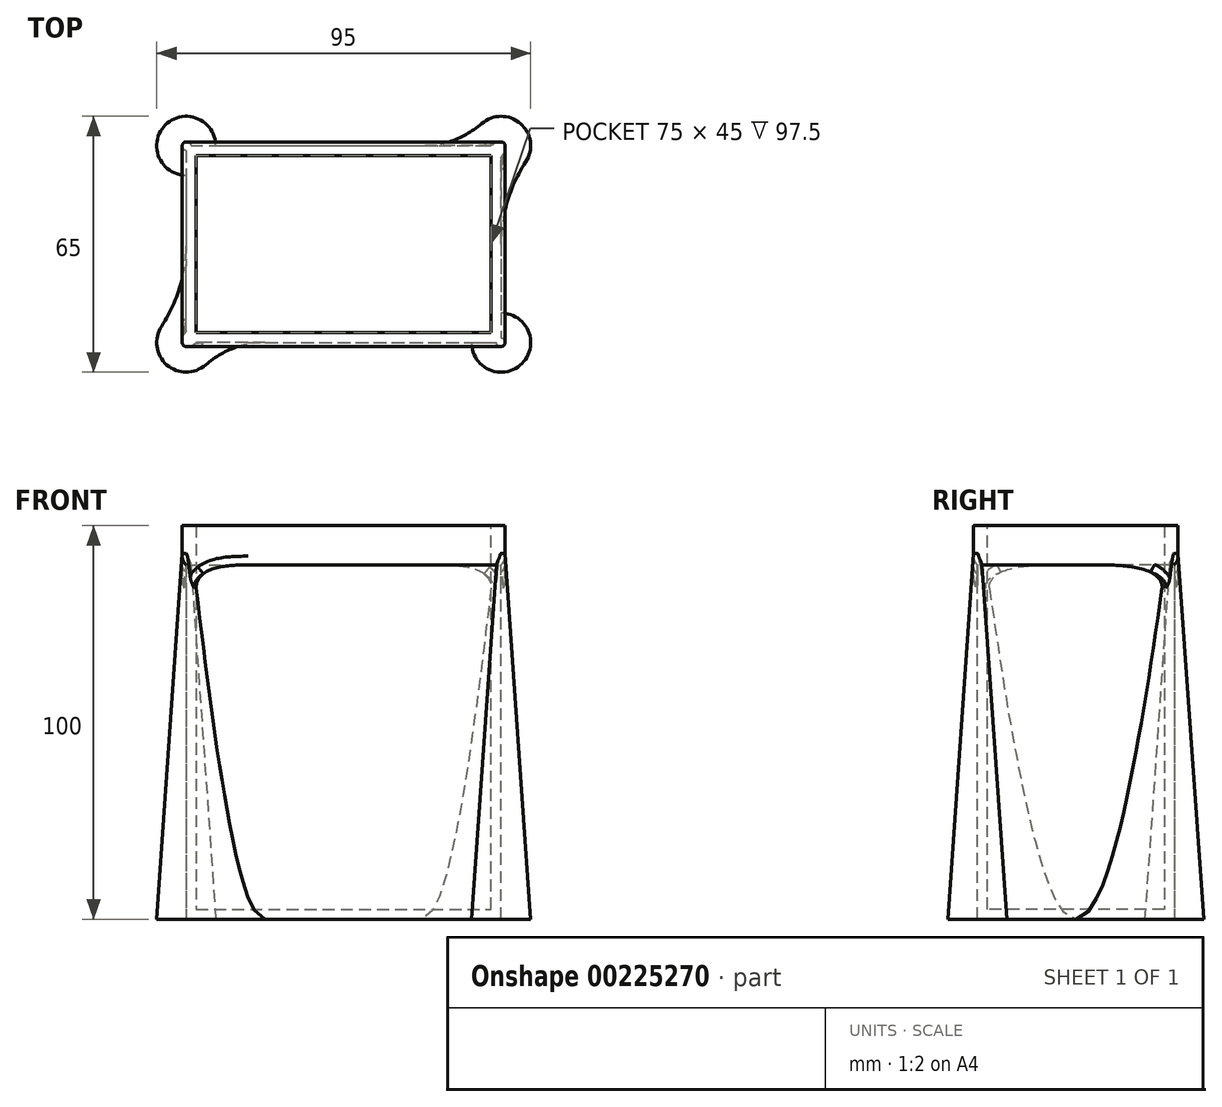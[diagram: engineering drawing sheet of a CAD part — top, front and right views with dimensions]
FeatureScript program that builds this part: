
annotation { "Feature Type Name" : "Feature", "Feature Type Description" : "" }
export const myFeature = defineFeature(function(context is Context, id is Id, definition is map)
    precondition{}
    {
        {
            var Q0;
            Q0=qCreatedBy(makeId("Top.planeOp"),FACE);
            var sketch = newSketch(context, id + "F0", { "sketchPlane" : qUnion([Q0])});
            skLineSegment(sketch, "E0.bottom", {"start": v(-40, 25) * mm, "end": v(40, 25) * mm});
            skLineSegment(sketch, "E0.top", {"start": v(-40, -25) * mm, "end": v(40, -25) * mm});
            skLineSegment(sketch, "E0.left", {"start": v(-40, 25) * mm, "end": v(-40, -25) * mm});
            skLineSegment(sketch, "E0.right", {"start": v(40, 25) * mm, "end": v(40, -25) * mm});
            skPoint(sketch, "E0.middle", {"position": v(0, 0) * mm});
            skSolve(sketch);
        }
        {
            var Q0;
            Q0 = qSketchRegion(id + "F0", true);
            extrude(context, id + "F1", {"entities" : qUnion([Q0]), "depth" : 100 * mm, "offsetDistance" : 25 * mm});
        }
        {
            var Q0;
            Q0=makeQuery(id+"F1.opExtrude","CAP_FACE",FACE,{"disambiguationData":[OSD([sQuery(id+"F0.wireOp",EDGE,"E0.bottom"),sQuery(id+"F0.wireOp",EDGE,"E0.top"),sQuery(id+"F0.wireOp",EDGE,"E0.left"),sQuery(id+"F0.wireOp",EDGE,"E0.right")])],"isStart":false});
            shell(context, id + "F2", {"entities" : qUnion([Q0]), "thickness" : 2.5 * mm});
        }
        {
            var Q0;
            Q0=makeQuery(id+"F1.opExtrude","CAP_FACE",FACE,{"disambiguationData":[OSD([sQuery(id+"F0.wireOp",EDGE,"E0.bottom"),sQuery(id+"F0.wireOp",EDGE,"E0.top"),sQuery(id+"F0.wireOp",EDGE,"E0.left"),sQuery(id+"F0.wireOp",EDGE,"E0.right")])],"isStart":true});
            var sketch = newSketch(context, id + "F3", { "sketchPlane" : qUnion([Q0])});
            skCircle(sketch, "E1", {"center": v(-40, 25) * mm, "radius": 7.5 * mm});
            skLineSegment(sketch, "E2", {"start": v(0, 34.3) * mm, "end": v(0, -35.51) * mm, "construction": true});
            skLineSegment(sketch, "E3", {"start": v(-69.58, 0) * mm, "end": v(52.99, 0) * mm, "construction": true});
            skArc(sketch, "E4", {"start": v(-40, 0) * mm, "mid": v(-41.6, 10.9) * mm, "end": v(-46.26, 20.87) * mm});
            skArc(sketch, "E5", {"start": v(-35.07, 30.65) * mm, "mid": v(-28.05, 26.46) * mm, "end": v(-20, 25) * mm});
            skCircle(sketch, "E6.MirrorC", {"center": v(40, 25) * mm, "radius": 7.5 * mm});
            skArc(sketch, "E7.MirrorCS", {"start": v(35.07, 30.65) * mm, "mid": v(28.05, 26.46) * mm, "end": v(20, 25) * mm});
            skArc(sketch, "E8.MirrorCS", {"start": v(40, 0) * mm, "mid": v(41.6, 10.9) * mm, "end": v(46.26, 20.87) * mm});
            skCircle(sketch, "E9.MirrorC", {"center": v(-40, -25) * mm, "radius": 7.5 * mm});
            skArc(sketch, "E10.MirrorCS", {"start": v(35.07, -30.65) * mm, "mid": v(28.05, -26.46) * mm, "end": v(20, -25) * mm});
            skCircle(sketch, "E11.MirrorC", {"center": v(40, -25) * mm, "radius": 7.5 * mm});
            skArc(sketch, "E12.MirrorCS", {"start": v(40, 0) * mm, "mid": v(41.6, -10.9) * mm, "end": v(46.26, -20.87) * mm});
            skArc(sketch, "E13.MirrorCS", {"start": v(-35.07, -30.65) * mm, "mid": v(-28.05, -26.46) * mm, "end": v(-20, -25) * mm});
            skArc(sketch, "E14.MirrorCS", {"start": v(-40, 0) * mm, "mid": v(-41.6, -10.9) * mm, "end": v(-46.26, -20.87) * mm});
            skSolve(sketch);
        }
        {
            var Q0;
            {var subQ0=makeQuery(id+"F1.opExtrude","CAP_EDGE",EDGE,{"disambiguationData":[OSD([sQuery(id+"F0.wireOp",EDGE,"E0.top")])],"isStart":true});var subQ5=sQuery(id+"F3.wireOp",EDGE,"E1");var subQ6=makeQuery(id+"F3.imprint","INTERSECT",VERTEX,{"derivedFrom":[subQ0,subQ5]});Q0=makeQuery(id+"F3.imprint","IMPRINT",FACE,{"disambiguationData":[TD([[makeQuery(id+"F3.imprint","IMPRINT",EDGE,{"disambiguationData":[TD([[subQ6,1.0]])],"derivedFrom":subQ5}),-1.0]])]});}
            cPlane(context, id + "F4", {"entities" : qUnion([Q0]), "cplaneType" : CPlaneType.OFFSET, "offset" : 67 * mm, "oppositeDirection" : true, "width" : 150 * mm, "height" : 150 * mm});
        }
        {
            var Q0;
            Q0 = qSketchRegion(id + "F3", true);
            var Q1;
            {var subQ0=sQuery(id+"F3.wireOp",EDGE,"E14.MirrorCS");Q1=makeQuery(id+"F3.imprint","IMPRINT",FACE,{"disambiguationData":[TD([[makeQuery(id+"F3.imprint","IMPRINT",EDGE,{"derivedFrom":subQ0}),1.0]])]});}
            var Q2;
            {var subQ0=makeQuery(id+"F1.opExtrude","CAP_EDGE",EDGE,{"disambiguationData":[OSD([sQuery(id+"F0.wireOp",EDGE,"E0.top")])],"isStart":true});var subQ5=sQuery(id+"F3.wireOp",EDGE,"E1");var subQ6=makeQuery(id+"F3.imprint","INTERSECT",VERTEX,{"derivedFrom":[subQ0,subQ5]});Q2=makeQuery(id+"F3.imprint","IMPRINT",FACE,{"disambiguationData":[TD([[makeQuery(id+"F3.imprint","IMPRINT",EDGE,{"disambiguationData":[TD([[subQ6,1.0]])],"derivedFrom":subQ5}),-1.0]])]});}
            var Q3;
            {var subQ0=sQuery(id+"F3.wireOp",EDGE,"E13.MirrorCS");Q3=makeQuery(id+"F3.imprint","IMPRINT",FACE,{"disambiguationData":[TD([[makeQuery(id+"F3.imprint","IMPRINT",EDGE,{"derivedFrom":subQ0}),1.0]])]});}
            var Q4;
            {var subQ0=sQuery(id+"F3.wireOp",EDGE,"E4");Q4=makeQuery(id+"F3.imprint","IMPRINT",FACE,{"disambiguationData":[TD([[makeQuery(id+"F3.imprint","IMPRINT",EDGE,{"derivedFrom":subQ0}),-1.0]])]});}
            var Q5;
            {var subQ0=sQuery(id+"F3.wireOp",EDGE,"E5");Q5=makeQuery(id+"F3.imprint","IMPRINT",FACE,{"disambiguationData":[TD([[makeQuery(id+"F3.imprint","IMPRINT",EDGE,{"derivedFrom":subQ0}),-1.0]])]});}
            var Q6;
            {var subQ0=sQuery(id+"F3.wireOp",EDGE,"E7.MirrorCS");Q6=makeQuery(id+"F3.imprint","IMPRINT",FACE,{"disambiguationData":[TD([[makeQuery(id+"F3.imprint","IMPRINT",EDGE,{"derivedFrom":subQ0}),1.0]])]});}
            var Q7;
            {var subQ0=sQuery(id+"F3.wireOp",EDGE,"E8.MirrorCS");Q7=makeQuery(id+"F3.imprint","IMPRINT",FACE,{"disambiguationData":[TD([[makeQuery(id+"F3.imprint","IMPRINT",EDGE,{"derivedFrom":subQ0}),1.0]])]});}
            var Q8;
            {var subQ0=sQuery(id+"F3.wireOp",EDGE,"E12.MirrorCS");Q8=makeQuery(id+"F3.imprint","IMPRINT",FACE,{"disambiguationData":[TD([[makeQuery(id+"F3.imprint","IMPRINT",EDGE,{"derivedFrom":subQ0}),-1.0]])]});}
            var Q9;
            {var subQ0=sQuery(id+"F3.wireOp",EDGE,"E10.MirrorCS");Q9=makeQuery(id+"F3.imprint","IMPRINT",FACE,{"disambiguationData":[TD([[makeQuery(id+"F3.imprint","IMPRINT",EDGE,{"derivedFrom":subQ0}),-1.0]])]});}
            extrude(context, id + "F5", {"entities" : qUnion([Q0, Q1, Q2, Q3, Q4, Q5, Q6, Q7, Q8, Q9]), "operationType" : NewBodyOperationType.ADD, "oppositeDirection" : true, "depth" : 100 * mm, "offsetDistance" : 25 * mm, "hasDraft" : true, "draftAngle" : 4 * degree, "draftPullDirection" : true});
        }
        {
            var Q0;
            {var subQ0=sQuery(id+"F0.wireOp",EDGE,"E0.top");var subQ1=sQuery(id+"F0.wireOp",EDGE,"E0.bottom");Q0=makeQuery(id+"F5.boolean.opBoolean","MERGE",FACE,{"derivedFrom":[makeQuery(id+"F1.opExtrude","CAP_FACE",FACE,{"disambiguationData":[OSD([subQ1,subQ0,sQuery(id+"F0.wireOp",EDGE,"E0.left"),sQuery(id+"F0.wireOp",EDGE,"E0.right")])],"isStart":false}),makeQuery(id+"F5.opExtrude","CAP_FACE",FACE,{"disambiguationData":[OSD([subQ1,subQ0,sQuery(id+"F3.wireOp",EDGE,"E1"),sQuery(id+"F3.wireOp",EDGE,"E4"),sQuery(id+"F3.wireOp",EDGE,"E5"),sQuery(id+"F3.wireOp",EDGE,"E6.MirrorC"),sQuery(id+"F3.wireOp",EDGE,"E7.MirrorCS"),sQuery(id+"F3.wireOp",EDGE,"E8.MirrorCS"),sQuery(id+"F3.wireOp",EDGE,"E9.MirrorC"),sQuery(id+"F3.wireOp",EDGE,"E10.MirrorCS"),sQuery(id+"F3.wireOp",EDGE,"E11.MirrorC"),sQuery(id+"F3.wireOp",EDGE,"E12.MirrorCS"),sQuery(id+"F3.wireOp",EDGE,"E13.MirrorCS"),sQuery(id+"F3.wireOp",EDGE,"E14.MirrorCS")])],"isStart":false})]});}
            var sketch = newSketch(context, id + "F6", { "sketchPlane" : qUnion([Q0])});
            skLineSegment(sketch, "E15.bottom", {"start": v(-37.5, 22.5) * mm, "end": v(37.5, 22.5) * mm});
            skLineSegment(sketch, "E15.top", {"start": v(-37.5, -22.5) * mm, "end": v(37.5, -22.5) * mm});
            skLineSegment(sketch, "E15.left", {"start": v(-37.5, 22.5) * mm, "end": v(-37.5, -22.5) * mm});
            skLineSegment(sketch, "E15.right", {"start": v(37.5, 22.5) * mm, "end": v(37.5, -22.5) * mm});
            skPoint(sketch, "E15.middle", {"position": v(0, 0) * mm});
            skSolve(sketch);
        }
        {
            var Q0;
            {var subQ11=sQuery(id+"F3.wireOp",EDGE,"E1");Q0=makeQuery(id+"F6.imprint","IMPRINT",FACE,{"disambiguationData":[TD([[makeQuery(id+"F6.imprint","IMPRINT",EDGE,{"derivedFrom":makeQuery(id+"F5.opExtrude","CAP_EDGE",EDGE,{"disambiguationData":[OSD([subQ11])],"isStart":false})}),-1.0]])]});}
            var sketch = newSketch(context, id + "F7", { "sketchPlane" : qUnion([Q0])});
            skLineSegment(sketch, "E16.bottom", {"start": v(-41, 26) * mm, "end": v(41, 26) * mm});
            skLineSegment(sketch, "E16.top", {"start": v(-41, -26) * mm, "end": v(41, -26) * mm});
            skLineSegment(sketch, "E16.left", {"start": v(-41, 26) * mm, "end": v(-41, -26) * mm});
            skLineSegment(sketch, "E16.right", {"start": v(41, 26) * mm, "end": v(41, -26) * mm});
            skSolve(sketch);
        }
        {
            var Q0;
            Q0 = qSketchRegion(id + "F7", true);
            extrude(context, id + "F8", {"entities" : qUnion([Q0]), "operationType" : NewBodyOperationType.ADD, "oppositeDirection" : true, "depth" : 10 * mm, "offsetDistance" : 25 * mm});
        }
        {
            var Q0;
            Q0=makeQuery(id+"F8.opExtrude","SWEPT_EDGE",EDGE,{"disambiguationData":[OSD([sQuery(id+"F7.wireOp",EDGE,"E16.top"),sQuery(id+"F7.wireOp",EDGE,"E16.left")])]});
            var Q1;
            Q1=makeQuery(id+"F8.opExtrude","SWEPT_EDGE",EDGE,{"disambiguationData":[OSD([sQuery(id+"F7.wireOp",EDGE,"E16.bottom"),sQuery(id+"F7.wireOp",EDGE,"E16.left")])]});
            var Q2;
            Q2=makeQuery(id+"F8.opExtrude","SWEPT_EDGE",EDGE,{"disambiguationData":[OSD([sQuery(id+"F7.wireOp",EDGE,"E16.top"),sQuery(id+"F7.wireOp",EDGE,"E16.right")])]});
            var Q3;
            Q3=makeQuery(id+"F8.opExtrude","SWEPT_EDGE",EDGE,{"disambiguationData":[OSD([sQuery(id+"F7.wireOp",EDGE,"E16.bottom"),sQuery(id+"F7.wireOp",EDGE,"E16.right")])]});
            fillet(context, id + "F9", {"entities" : qUnion([Q0, Q1, Q2, Q3]), "radius" : 1 * mm, "tangentPropagation" : true, "allowEdgeOverflow" : false});
        }
        {
            var Q0;
            {var subQ1=sQuery(id+"F3.wireOp",EDGE,"E1");var subQ5=sQuery(id+"F3.wireOp",EDGE,"E14.MirrorCS");var subQ15=sQuery(id+"F3.wireOp",EDGE,"E4");var subQ16=makeQuery(id+"F5.opExtrude","SWEPT_FACE",FACE,{"disambiguationData":[OSD([subQ15,subQ5])]});Q0=makeQuery(id+"F8.boolean.opBoolean","INTERSECT",EDGE,{"derivedFrom":[makeQuery(id+"F5.boolean.opBoolean","SPLIT",FACE,{"disambiguationData":[TD([makeQuery(id+"F5.opExtrude","SWEPT_FACE",FACE,{"disambiguationData":[OSD([subQ1])]})])],"derivedFrom":subQ16}),makeQuery(id+"F8.opExtrude","CAP_FACE",FACE,{"disambiguationData":[OSD([sQuery(id+"F7.wireOp",EDGE,"E16.bottom"),sQuery(id+"F7.wireOp",EDGE,"E16.top"),sQuery(id+"F7.wireOp",EDGE,"E16.left"),sQuery(id+"F7.wireOp",EDGE,"E16.right")])],"isStart":false})]});}
            var Q1;
            {var subQ0=sQuery(id+"F3.wireOp",EDGE,"E14.MirrorCS");var subQ5=sQuery(id+"F3.wireOp",EDGE,"E9.MirrorC");var subQ10=sQuery(id+"F3.wireOp",EDGE,"E4");var subQ16=makeQuery(id+"F5.opExtrude","SWEPT_FACE",FACE,{"disambiguationData":[OSD([subQ10,subQ0])]});Q1=makeQuery(id+"F8.boolean.opBoolean","INTERSECT",EDGE,{"derivedFrom":[makeQuery(id+"F5.boolean.opBoolean","SPLIT",FACE,{"disambiguationData":[TD([makeQuery(id+"F5.opExtrude","SWEPT_FACE",FACE,{"disambiguationData":[OSD([subQ5])]})])],"derivedFrom":subQ16}),makeQuery(id+"F8.opExtrude","CAP_FACE",FACE,{"disambiguationData":[OSD([sQuery(id+"F7.wireOp",EDGE,"E16.bottom"),sQuery(id+"F7.wireOp",EDGE,"E16.top"),sQuery(id+"F7.wireOp",EDGE,"E16.left"),sQuery(id+"F7.wireOp",EDGE,"E16.right")])],"isStart":false})]});}
            var Q2;
            {var subQ7=sQuery(id+"F3.wireOp",EDGE,"E7.MirrorCS");var subQ12=sQuery(id+"F0.wireOp",EDGE,"E0.top");Q2=makeQuery(id+"F8.boolean.opBoolean","INTERSECT",EDGE,{"derivedFrom":[makeQuery(id+"F5.boolean.opBoolean","SPLIT",FACE,{"disambiguationData":[TD([makeQuery(id+"F1.opExtrude","SWEPT_FACE",FACE,{"disambiguationData":[OSD([subQ12])]})])],"derivedFrom":makeQuery(id+"F5.opExtrude","SWEPT_FACE",FACE,{"disambiguationData":[OSD([subQ7])]})}),makeQuery(id+"F8.opExtrude","CAP_FACE",FACE,{"disambiguationData":[OSD([sQuery(id+"F7.wireOp",EDGE,"E16.bottom"),sQuery(id+"F7.wireOp",EDGE,"E16.top"),sQuery(id+"F7.wireOp",EDGE,"E16.left"),sQuery(id+"F7.wireOp",EDGE,"E16.right")])],"isStart":false})]});}
            var Q3;
            {var subQ0=sQuery(id+"F0.wireOp",EDGE,"E0.top");var subQ14=sQuery(id+"F3.wireOp",EDGE,"E5");Q3=makeQuery(id+"F8.boolean.opBoolean","INTERSECT",EDGE,{"derivedFrom":[makeQuery(id+"F5.boolean.opBoolean","SPLIT",FACE,{"disambiguationData":[TD([makeQuery(id+"F1.opExtrude","SWEPT_FACE",FACE,{"disambiguationData":[OSD([subQ0])]})])],"derivedFrom":makeQuery(id+"F5.opExtrude","SWEPT_FACE",FACE,{"disambiguationData":[OSD([subQ14])]})}),makeQuery(id+"F8.opExtrude","CAP_FACE",FACE,{"disambiguationData":[OSD([sQuery(id+"F7.wireOp",EDGE,"E16.bottom"),sQuery(id+"F7.wireOp",EDGE,"E16.top"),sQuery(id+"F7.wireOp",EDGE,"E16.left"),sQuery(id+"F7.wireOp",EDGE,"E16.right")])],"isStart":false})]});}
            var Q4;
            {var subQ2=sQuery(id+"F3.wireOp",EDGE,"E12.MirrorCS");var subQ6=sQuery(id+"F3.wireOp",EDGE,"E8.MirrorCS");var subQ8=sQuery(id+"F3.wireOp",EDGE,"E6.MirrorC");var subQ16=makeQuery(id+"F5.opExtrude","SWEPT_FACE",FACE,{"disambiguationData":[OSD([subQ6,subQ2])]});Q4=makeQuery(id+"F8.boolean.opBoolean","INTERSECT",EDGE,{"derivedFrom":[makeQuery(id+"F5.boolean.opBoolean","SPLIT",FACE,{"disambiguationData":[TD([makeQuery(id+"F5.opExtrude","SWEPT_FACE",FACE,{"disambiguationData":[OSD([subQ8])]})])],"derivedFrom":subQ16}),makeQuery(id+"F8.opExtrude","CAP_FACE",FACE,{"disambiguationData":[OSD([sQuery(id+"F7.wireOp",EDGE,"E16.bottom"),sQuery(id+"F7.wireOp",EDGE,"E16.top"),sQuery(id+"F7.wireOp",EDGE,"E16.left"),sQuery(id+"F7.wireOp",EDGE,"E16.right")])],"isStart":false})]});}
            var Q5;
            {var subQ2=sQuery(id+"F3.wireOp",EDGE,"E12.MirrorCS");var subQ3=sQuery(id+"F3.wireOp",EDGE,"E11.MirrorC");var subQ6=sQuery(id+"F3.wireOp",EDGE,"E8.MirrorCS");var subQ16=makeQuery(id+"F5.opExtrude","SWEPT_FACE",FACE,{"disambiguationData":[OSD([subQ6,subQ2])]});Q5=makeQuery(id+"F8.boolean.opBoolean","INTERSECT",EDGE,{"derivedFrom":[makeQuery(id+"F5.boolean.opBoolean","SPLIT",FACE,{"disambiguationData":[TD([makeQuery(id+"F5.opExtrude","SWEPT_FACE",FACE,{"disambiguationData":[OSD([subQ3])]})])],"derivedFrom":subQ16}),makeQuery(id+"F8.opExtrude","CAP_FACE",FACE,{"disambiguationData":[OSD([sQuery(id+"F7.wireOp",EDGE,"E16.bottom"),sQuery(id+"F7.wireOp",EDGE,"E16.top"),sQuery(id+"F7.wireOp",EDGE,"E16.left"),sQuery(id+"F7.wireOp",EDGE,"E16.right")])],"isStart":false})]});}
            var Q6;
            {var subQ4=sQuery(id+"F3.wireOp",EDGE,"E10.MirrorCS");var subQ13=sQuery(id+"F0.wireOp",EDGE,"E0.bottom");Q6=makeQuery(id+"F8.boolean.opBoolean","INTERSECT",EDGE,{"derivedFrom":[makeQuery(id+"F5.boolean.opBoolean","SPLIT",FACE,{"disambiguationData":[TD([makeQuery(id+"F1.opExtrude","SWEPT_FACE",FACE,{"disambiguationData":[OSD([subQ13])]})])],"derivedFrom":makeQuery(id+"F5.opExtrude","SWEPT_FACE",FACE,{"disambiguationData":[OSD([subQ4])]})}),makeQuery(id+"F8.opExtrude","CAP_FACE",FACE,{"disambiguationData":[OSD([sQuery(id+"F7.wireOp",EDGE,"E16.bottom"),sQuery(id+"F7.wireOp",EDGE,"E16.top"),sQuery(id+"F7.wireOp",EDGE,"E16.left"),sQuery(id+"F7.wireOp",EDGE,"E16.right")])],"isStart":false})]});}
            var Q7;
            {var subQ1=sQuery(id+"F3.wireOp",EDGE,"E13.MirrorCS");var subQ13=sQuery(id+"F0.wireOp",EDGE,"E0.bottom");Q7=makeQuery(id+"F8.boolean.opBoolean","INTERSECT",EDGE,{"derivedFrom":[makeQuery(id+"F5.boolean.opBoolean","SPLIT",FACE,{"disambiguationData":[TD([makeQuery(id+"F1.opExtrude","SWEPT_FACE",FACE,{"disambiguationData":[OSD([subQ13])]})])],"derivedFrom":makeQuery(id+"F5.opExtrude","SWEPT_FACE",FACE,{"disambiguationData":[OSD([subQ1])]})}),makeQuery(id+"F8.opExtrude","CAP_FACE",FACE,{"disambiguationData":[OSD([sQuery(id+"F7.wireOp",EDGE,"E16.bottom"),sQuery(id+"F7.wireOp",EDGE,"E16.top"),sQuery(id+"F7.wireOp",EDGE,"E16.left"),sQuery(id+"F7.wireOp",EDGE,"E16.right")])],"isStart":false})]});}
            fillet(context, id + "F10", {"entities" : qUnion([Q0, Q1, Q2, Q3, Q4, Q5, Q6, Q7]), "radius" : 5.5 * mm, "tangentPropagation" : true, "allowEdgeOverflow" : false});
        }
        {
            var Q0;
            {var subQ0=sQuery(id+"F7.wireOp",EDGE,"E16.left");var subQ1=sQuery(id+"F3.wireOp",EDGE,"E14.MirrorCS");var subQ6=sQuery(id+"F3.wireOp",EDGE,"E9.MirrorC");var subQ11=sQuery(id+"F3.wireOp",EDGE,"E4");var subQ17=makeQuery(id+"F5.opExtrude","SWEPT_FACE",FACE,{"disambiguationData":[OSD([subQ11,subQ1])]});Q0=makeQuery(id+"F10.opFillet","BLEND_EDGE",EDGE,{"blendedFrom":[makeQuery(id+"F8.boolean.opBoolean","INTERSECT",EDGE,{"derivedFrom":[makeQuery(id+"F5.boolean.opBoolean","SPLIT",FACE,{"disambiguationData":[TD([makeQuery(id+"F5.opExtrude","SWEPT_FACE",FACE,{"disambiguationData":[OSD([subQ6])]})])],"derivedFrom":subQ17}),makeQuery(id+"F8.opExtrude","CAP_FACE",FACE,{"disambiguationData":[OSD([sQuery(id+"F7.wireOp",EDGE,"E16.bottom"),sQuery(id+"F7.wireOp",EDGE,"E16.top"),subQ0,sQuery(id+"F7.wireOp",EDGE,"E16.right")])],"isStart":false})]}),makeQuery(id+"F8.opExtrude","SWEPT_FACE",FACE,{"disambiguationData":[OSD([subQ0])]})],"blendedInto":[makeQuery(id+"F8.opExtrude","SWEPT_FACE",FACE,{"disambiguationData":[OSD([subQ0])]})]});}
            var Q1;
            {var subQ0=sQuery(id+"F7.wireOp",EDGE,"E16.left");var subQ2=sQuery(id+"F3.wireOp",EDGE,"E1");var subQ6=sQuery(id+"F3.wireOp",EDGE,"E14.MirrorCS");var subQ16=sQuery(id+"F3.wireOp",EDGE,"E4");var subQ17=makeQuery(id+"F5.opExtrude","SWEPT_FACE",FACE,{"disambiguationData":[OSD([subQ16,subQ6])]});Q1=makeQuery(id+"F10.opFillet","BLEND_EDGE",EDGE,{"blendedFrom":[makeQuery(id+"F8.boolean.opBoolean","INTERSECT",EDGE,{"derivedFrom":[makeQuery(id+"F5.boolean.opBoolean","SPLIT",FACE,{"disambiguationData":[TD([makeQuery(id+"F5.opExtrude","SWEPT_FACE",FACE,{"disambiguationData":[OSD([subQ2])]})])],"derivedFrom":subQ17}),makeQuery(id+"F8.opExtrude","CAP_FACE",FACE,{"disambiguationData":[OSD([sQuery(id+"F7.wireOp",EDGE,"E16.bottom"),sQuery(id+"F7.wireOp",EDGE,"E16.top"),subQ0,sQuery(id+"F7.wireOp",EDGE,"E16.right")])],"isStart":false})]}),makeQuery(id+"F8.opExtrude","SWEPT_FACE",FACE,{"disambiguationData":[OSD([subQ0])]})],"blendedInto":[makeQuery(id+"F8.opExtrude","SWEPT_FACE",FACE,{"disambiguationData":[OSD([subQ0])]})]});}
            var Q2;
            {var subQ0=sQuery(id+"F7.wireOp",EDGE,"E16.left");Q2=makeQuery(id+"F8.boolean.opBoolean","SPLIT",EDGE,{"disambiguationData":[TD([makeQuery(id+"F5.opExtrude","SWEPT_FACE",FACE,{"disambiguationData":[OSD([sQuery(id+"F3.wireOp",EDGE,"E4"),sQuery(id+"F3.wireOp",EDGE,"E14.MirrorCS")])]})])],"derivedFrom":makeQuery(id+"F8.opExtrude","CAP_EDGE",EDGE,{"disambiguationData":[OSD([subQ0])],"isStart":false})});}
            var Q3;
            {var subQ0=sQuery(id+"F7.wireOp",EDGE,"E16.top");var subQ1=sQuery(id+"F0.wireOp",EDGE,"E0.top");var subQ15=sQuery(id+"F3.wireOp",EDGE,"E5");Q3=makeQuery(id+"F10.opFillet","BLEND_EDGE",EDGE,{"blendedFrom":[makeQuery(id+"F8.boolean.opBoolean","INTERSECT",EDGE,{"derivedFrom":[makeQuery(id+"F5.boolean.opBoolean","SPLIT",FACE,{"disambiguationData":[TD([makeQuery(id+"F1.opExtrude","SWEPT_FACE",FACE,{"disambiguationData":[OSD([subQ1])]})])],"derivedFrom":makeQuery(id+"F5.opExtrude","SWEPT_FACE",FACE,{"disambiguationData":[OSD([subQ15])]})}),makeQuery(id+"F8.opExtrude","CAP_FACE",FACE,{"disambiguationData":[OSD([sQuery(id+"F7.wireOp",EDGE,"E16.bottom"),subQ0,sQuery(id+"F7.wireOp",EDGE,"E16.left"),sQuery(id+"F7.wireOp",EDGE,"E16.right")])],"isStart":false})]}),makeQuery(id+"F8.opExtrude","SWEPT_FACE",FACE,{"disambiguationData":[OSD([subQ0])]})],"blendedInto":[makeQuery(id+"F8.opExtrude","SWEPT_FACE",FACE,{"disambiguationData":[OSD([subQ0])]})]});}
            var Q4;
            {var subQ0=sQuery(id+"F7.wireOp",EDGE,"E16.top");Q4=makeQuery(id+"F8.boolean.opBoolean","SPLIT",EDGE,{"disambiguationData":[TD([makeQuery(id+"F5.opExtrude","SWEPT_FACE",FACE,{"disambiguationData":[OSD([sQuery(id+"F3.wireOp",EDGE,"E1")])]}),makeQuery(id+"F5.opExtrude","SWEPT_FACE",FACE,{"disambiguationData":[OSD([sQuery(id+"F3.wireOp",EDGE,"E6.MirrorC")])]}),makeQuery(id+"F8.opExtrude","CAP_FACE",FACE,{"disambiguationData":[OSD([sQuery(id+"F7.wireOp",EDGE,"E16.bottom"),subQ0,sQuery(id+"F7.wireOp",EDGE,"E16.left"),sQuery(id+"F7.wireOp",EDGE,"E16.right")])],"isStart":false}),makeQuery(id+"F8.opExtrude","SWEPT_FACE",FACE,{"disambiguationData":[OSD([subQ0])]})])],"derivedFrom":makeQuery(id+"F8.opExtrude","CAP_EDGE",EDGE,{"disambiguationData":[OSD([subQ0])],"isStart":false})});}
            var Q5;
            {var subQ0=sQuery(id+"F7.wireOp",EDGE,"E16.top");var subQ8=sQuery(id+"F3.wireOp",EDGE,"E7.MirrorCS");var subQ13=sQuery(id+"F0.wireOp",EDGE,"E0.top");Q5=makeQuery(id+"F10.opFillet","BLEND_EDGE",EDGE,{"blendedFrom":[makeQuery(id+"F8.boolean.opBoolean","INTERSECT",EDGE,{"derivedFrom":[makeQuery(id+"F5.boolean.opBoolean","SPLIT",FACE,{"disambiguationData":[TD([makeQuery(id+"F1.opExtrude","SWEPT_FACE",FACE,{"disambiguationData":[OSD([subQ13])]})])],"derivedFrom":makeQuery(id+"F5.opExtrude","SWEPT_FACE",FACE,{"disambiguationData":[OSD([subQ8])]})}),makeQuery(id+"F8.opExtrude","CAP_FACE",FACE,{"disambiguationData":[OSD([sQuery(id+"F7.wireOp",EDGE,"E16.bottom"),subQ0,sQuery(id+"F7.wireOp",EDGE,"E16.left"),sQuery(id+"F7.wireOp",EDGE,"E16.right")])],"isStart":false})]}),makeQuery(id+"F8.opExtrude","SWEPT_FACE",FACE,{"disambiguationData":[OSD([subQ0])]})],"blendedInto":[makeQuery(id+"F8.opExtrude","SWEPT_FACE",FACE,{"disambiguationData":[OSD([subQ0])]})]});}
            var Q6;
            {var subQ0=sQuery(id+"F7.wireOp",EDGE,"E16.right");var subQ3=sQuery(id+"F3.wireOp",EDGE,"E12.MirrorCS");var subQ7=sQuery(id+"F3.wireOp",EDGE,"E8.MirrorCS");var subQ9=sQuery(id+"F3.wireOp",EDGE,"E6.MirrorC");var subQ17=makeQuery(id+"F5.opExtrude","SWEPT_FACE",FACE,{"disambiguationData":[OSD([subQ7,subQ3])]});Q6=makeQuery(id+"F10.opFillet","BLEND_EDGE",EDGE,{"blendedFrom":[makeQuery(id+"F8.boolean.opBoolean","INTERSECT",EDGE,{"derivedFrom":[makeQuery(id+"F5.boolean.opBoolean","SPLIT",FACE,{"disambiguationData":[TD([makeQuery(id+"F5.opExtrude","SWEPT_FACE",FACE,{"disambiguationData":[OSD([subQ9])]})])],"derivedFrom":subQ17}),makeQuery(id+"F8.opExtrude","CAP_FACE",FACE,{"disambiguationData":[OSD([sQuery(id+"F7.wireOp",EDGE,"E16.bottom"),sQuery(id+"F7.wireOp",EDGE,"E16.top"),sQuery(id+"F7.wireOp",EDGE,"E16.left"),subQ0])],"isStart":false})]}),makeQuery(id+"F8.opExtrude","SWEPT_FACE",FACE,{"disambiguationData":[OSD([subQ0])]})],"blendedInto":[makeQuery(id+"F8.opExtrude","SWEPT_FACE",FACE,{"disambiguationData":[OSD([subQ0])]})]});}
            var Q7;
            {var subQ0=sQuery(id+"F7.wireOp",EDGE,"E16.right");Q7=makeQuery(id+"F8.boolean.opBoolean","SPLIT",EDGE,{"disambiguationData":[TD([makeQuery(id+"F5.opExtrude","SWEPT_FACE",FACE,{"disambiguationData":[OSD([sQuery(id+"F3.wireOp",EDGE,"E8.MirrorCS"),sQuery(id+"F3.wireOp",EDGE,"E12.MirrorCS")])]})])],"derivedFrom":makeQuery(id+"F8.opExtrude","CAP_EDGE",EDGE,{"disambiguationData":[OSD([subQ0])],"isStart":false})});}
            var Q8;
            {var subQ0=sQuery(id+"F7.wireOp",EDGE,"E16.right");var subQ3=sQuery(id+"F3.wireOp",EDGE,"E12.MirrorCS");var subQ4=sQuery(id+"F3.wireOp",EDGE,"E11.MirrorC");var subQ7=sQuery(id+"F3.wireOp",EDGE,"E8.MirrorCS");var subQ17=makeQuery(id+"F5.opExtrude","SWEPT_FACE",FACE,{"disambiguationData":[OSD([subQ7,subQ3])]});Q8=makeQuery(id+"F10.opFillet","BLEND_EDGE",EDGE,{"blendedFrom":[makeQuery(id+"F8.boolean.opBoolean","INTERSECT",EDGE,{"derivedFrom":[makeQuery(id+"F5.boolean.opBoolean","SPLIT",FACE,{"disambiguationData":[TD([makeQuery(id+"F5.opExtrude","SWEPT_FACE",FACE,{"disambiguationData":[OSD([subQ4])]})])],"derivedFrom":subQ17}),makeQuery(id+"F8.opExtrude","CAP_FACE",FACE,{"disambiguationData":[OSD([sQuery(id+"F7.wireOp",EDGE,"E16.bottom"),sQuery(id+"F7.wireOp",EDGE,"E16.top"),sQuery(id+"F7.wireOp",EDGE,"E16.left"),subQ0])],"isStart":false})]}),makeQuery(id+"F8.opExtrude","SWEPT_FACE",FACE,{"disambiguationData":[OSD([subQ0])]})],"blendedInto":[makeQuery(id+"F8.opExtrude","SWEPT_FACE",FACE,{"disambiguationData":[OSD([subQ0])]})]});}
            var Q9;
            {var subQ0=sQuery(id+"F7.wireOp",EDGE,"E16.bottom");var subQ2=sQuery(id+"F3.wireOp",EDGE,"E13.MirrorCS");var subQ14=sQuery(id+"F0.wireOp",EDGE,"E0.bottom");Q9=makeQuery(id+"F10.opFillet","BLEND_EDGE",EDGE,{"blendedFrom":[makeQuery(id+"F8.boolean.opBoolean","INTERSECT",EDGE,{"derivedFrom":[makeQuery(id+"F5.boolean.opBoolean","SPLIT",FACE,{"disambiguationData":[TD([makeQuery(id+"F1.opExtrude","SWEPT_FACE",FACE,{"disambiguationData":[OSD([subQ14])]})])],"derivedFrom":makeQuery(id+"F5.opExtrude","SWEPT_FACE",FACE,{"disambiguationData":[OSD([subQ2])]})}),makeQuery(id+"F8.opExtrude","CAP_FACE",FACE,{"disambiguationData":[OSD([subQ0,sQuery(id+"F7.wireOp",EDGE,"E16.top"),sQuery(id+"F7.wireOp",EDGE,"E16.left"),sQuery(id+"F7.wireOp",EDGE,"E16.right")])],"isStart":false})]}),makeQuery(id+"F8.opExtrude","SWEPT_FACE",FACE,{"disambiguationData":[OSD([subQ0])]})],"blendedInto":[makeQuery(id+"F8.opExtrude","SWEPT_FACE",FACE,{"disambiguationData":[OSD([subQ0])]})]});}
            var Q10;
            {var subQ0=sQuery(id+"F7.wireOp",EDGE,"E16.bottom");var subQ5=sQuery(id+"F3.wireOp",EDGE,"E10.MirrorCS");var subQ14=sQuery(id+"F0.wireOp",EDGE,"E0.bottom");Q10=makeQuery(id+"F10.opFillet","BLEND_EDGE",EDGE,{"blendedFrom":[makeQuery(id+"F8.boolean.opBoolean","INTERSECT",EDGE,{"derivedFrom":[makeQuery(id+"F5.boolean.opBoolean","SPLIT",FACE,{"disambiguationData":[TD([makeQuery(id+"F1.opExtrude","SWEPT_FACE",FACE,{"disambiguationData":[OSD([subQ14])]})])],"derivedFrom":makeQuery(id+"F5.opExtrude","SWEPT_FACE",FACE,{"disambiguationData":[OSD([subQ5])]})}),makeQuery(id+"F8.opExtrude","CAP_FACE",FACE,{"disambiguationData":[OSD([subQ0,sQuery(id+"F7.wireOp",EDGE,"E16.top"),sQuery(id+"F7.wireOp",EDGE,"E16.left"),sQuery(id+"F7.wireOp",EDGE,"E16.right")])],"isStart":false})]}),makeQuery(id+"F8.opExtrude","SWEPT_FACE",FACE,{"disambiguationData":[OSD([subQ0])]})],"blendedInto":[makeQuery(id+"F8.opExtrude","SWEPT_FACE",FACE,{"disambiguationData":[OSD([subQ0])]})]});}
            var Q11;
            {var subQ0=sQuery(id+"F7.wireOp",EDGE,"E16.bottom");Q11=makeQuery(id+"F8.boolean.opBoolean","SPLIT",EDGE,{"disambiguationData":[TD([makeQuery(id+"F5.opExtrude","SWEPT_FACE",FACE,{"disambiguationData":[OSD([sQuery(id+"F3.wireOp",EDGE,"E9.MirrorC")])]}),makeQuery(id+"F5.opExtrude","SWEPT_FACE",FACE,{"disambiguationData":[OSD([sQuery(id+"F3.wireOp",EDGE,"E11.MirrorC")])]}),makeQuery(id+"F8.opExtrude","SWEPT_FACE",FACE,{"disambiguationData":[OSD([subQ0])]}),makeQuery(id+"F8.opExtrude","CAP_FACE",FACE,{"disambiguationData":[OSD([subQ0,sQuery(id+"F7.wireOp",EDGE,"E16.top"),sQuery(id+"F7.wireOp",EDGE,"E16.left"),sQuery(id+"F7.wireOp",EDGE,"E16.right")])],"isStart":false})])],"derivedFrom":makeQuery(id+"F8.opExtrude","CAP_EDGE",EDGE,{"disambiguationData":[OSD([subQ0])],"isStart":false})});}
            fillet(context, id + "F11", {"entities" : qUnion([Q0, Q1, Q2, Q3, Q4, Q5, Q6, Q7, Q8, Q9, Q10, Q11]), "radius" : 3 * mm, "tangentPropagation" : true, "allowEdgeOverflow" : false});
        }
        {
            var Q0;
            Q0 = qSketchRegion(id + "F6", true);
            extrude(context, id + "F12", {"entities" : qUnion([Q0]), "operationType" : NewBodyOperationType.REMOVE, "oppositeDirection" : true, "depth" : 97.5 * mm, "offsetDistance" : 25 * mm});
        }
    });
